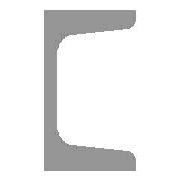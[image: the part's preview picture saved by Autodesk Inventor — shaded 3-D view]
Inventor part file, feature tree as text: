
AUTODESK INVENTOR PART (.ipt)
format: ipt  version: 2024 (Build 280153000, 153)  size: 135,168 bytes
history: native  units: mm (DEFAULTED — no unit token found)
features: other x3, extrude x1, sketch x1, plane x1
ambient origin geometry x8: Origin, YZ Plane, XZ Plane, XY Plane, X Axis, Y Axis, Z Axis, Center Point
bodies: Solid1 (feature_tree)
feature tree (6):
  other  "Driven Length"
  other  "Начальная плоскость"
  other  "Конечная плоскость"
  extrude  "Базовый элемент"  Depth=25.0mm
  sketch  "Sketch3"  dims[d0=5.0mm d1=25.0mm d2=25.0mm d3=6.0mm d4=12.5mm d5=1.0mm d6=30.0mm d7=0.0mm d23=6.0mm d24=3.0mm d25=0.0mm d26=-0.0mm d27=30.0mm d28=90.0deg d29=30.0mm]
  plane  "Work Plane3"
